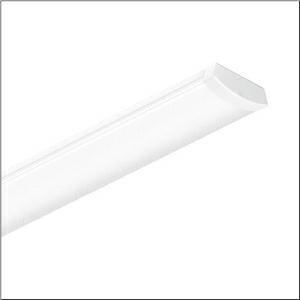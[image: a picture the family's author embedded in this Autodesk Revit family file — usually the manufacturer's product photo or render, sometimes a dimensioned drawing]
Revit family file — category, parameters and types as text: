
# Revit family: siluette_r__21_51ln12mdm20a_d267
name_source: partatom
category: Lighting Fixtures
units: mm (PartAtom-declared; Revit-internal decimal feet)

## family parameters
Cut with Voids When Loaded = No
Host = Face
Light Source = No
Part Type = Normal
Room Calculation Point = No
Round Connector Dimension = Use Diameter
Shared = No

## types (1)
- --- (1 x LED, 1510 lm, 12.2 W, 5000K)
    Apparent Load = 12 VA
    CIE Flux Codes = 43 73 92 94 100
    Color Rendering = 80
    Color Temperature = 5000K
    Default Elevation = 1800 mm
    Description = Siluette® 21, office luminaire, primary optical cover: enclosure, of PC, frosted, light emission: direct distribution, primary light characteristic: symmetric, installation type: suspended mounting, surface-mounted, LED, rated luminous flux: 2.630lm, luminous efficacy: 135lm/W, light colour: 830/840/850, colour temperature: 3000/4000/5000K, control gear: ON/OFF Multilumen, with terminal, 3-pole, mains connection: 220..240V, AC, 50/60Hz, rated input power: 20W, housing, of sheet steel, white, length: 600mm, width: 152mm, height: 53mm, end cap, of PMMA, white, protection rating (complete): IP44, insulation class (complete): insulation class I (protective earthing), certification: CE, UKCA, protection symbol: D, impact resistance: IK04, permissible operating ambient temperature: -20..+40°C, contact your sales advisor before using the luminaires in applications with unclear chemical exposure, large temperature fluctuations or condensation-forming humidity, corresponds to IFS (International Featured Standards) requirements for safety and quality in the food industry, packaging unit: 1 piece
    Height = 52 mm  [stored 0.170604 ft]
    Lamp = 1 x LED
    Lamp Light Flux = 1510 lm
    Lamp Power = 12.2 W
    Lamp count = 1
    Length = 645 mm
    Luminous efficacy = 124 lm/W
    Manufacturer = Siteco
    ModVariant = No
    Model = 51LN12MDM20A
    Mounting Place = Ceiling
    Mounting Type = Pendant
    Number of Poles = 1
    OnlyDefault = Yes
    Power Factor = 1
    Product Name = Siluette® 21
    Product group = office luminaire | ceiling pendant
    ProductGroupID = 903
    Protection Class = Protection class I
    Protection Degree = IP 44
    RLX_Detail_Level = 1
    RLX_Emergency_Light_Flux = 0 lm
    RLX_Emergency_Type = 0
    RLX_Emergency_Type_DB = No
    RlxData = <blob elided: 19181 chars, md5=6168270a>
    Socket = socket
    Standby Power = 0 W
    System Light Flux = 1510 lm
    System Power = 12 W
    Type Comments = individual setting: colour temperature 5000K, luminous flux: 58 % | (OFF | OFF | ON) | 200 mA
    Type Image = l_1296910.jpg
    URL = http://relux.com
    VarID = @adj_079577
    Voltage = 0 V
    Weight = 0.00 kg
    Width = 152 mm

note: [stored X ft] marks values corroborated as IEEE doubles in the binary element streams (Revit-internal decimal feet)

## geometry (parser evidence)
native form markers: Blend x4, Sweep x15
no freeform markers — native parametric forms only
